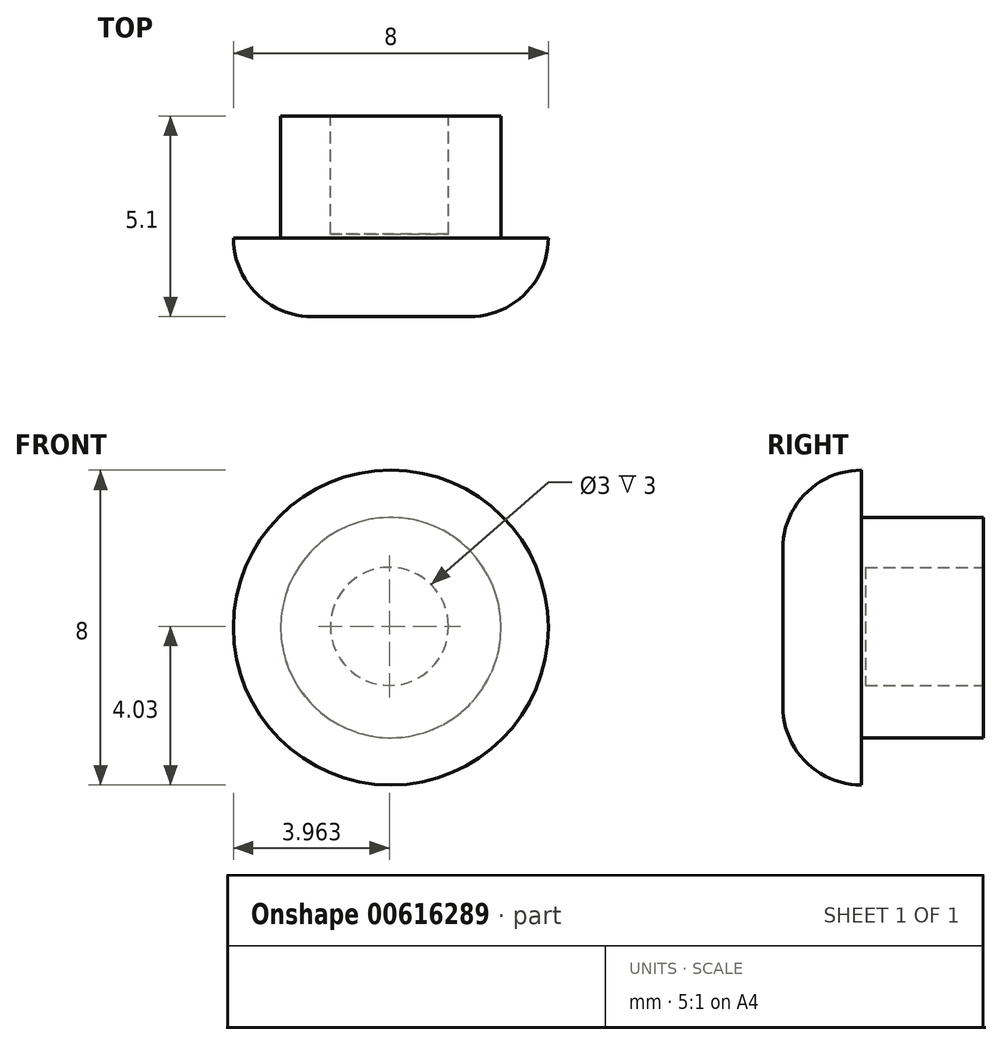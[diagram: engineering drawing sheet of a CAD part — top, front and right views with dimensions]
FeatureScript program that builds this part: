
annotation { "Feature Type Name" : "Feature", "Feature Type Description" : "" }
export const myFeature = defineFeature(function(context is Context, id is Id, definition is map)
    precondition{}
    {
        {
            var Q0;
            Q0=qCreatedBy(makeId("Front.planeOp"),FACE);
            var sketch = newSketch(context, id + "F0", { "sketchPlane" : qUnion([Q0])});
            skCircle(sketch, "E0", {"center": v(0, 0) * mm, "radius": 4 * mm});
            skSolve(sketch);
        }
        {
            var Q0;
            Q0=makeQuery(id+"F0.imprint","IMPRINT",FACE,{"disambiguationData":[TD([[makeQuery(id+"F0.imprint","IMPRINT",EDGE,{"derivedFrom":sQuery(id+"F0.wireOp",EDGE,"E0")}),1.0]])]});
            extrude(context, id + "F1", {"entities" : qUnion([Q0]), "depth" : 2 * mm, "offsetDistance" : 25 * mm});
        }
        {
            var Q0;
            Q0=makeQuery(id+"F1.opExtrude","CAP_EDGE",EDGE,{"disambiguationData":[OSD([sQuery(id+"F0.wireOp",EDGE,"E0")])],"isStart":false});
            fillet(context, id + "F2", {"entities" : qUnion([Q0]), "radius" : 2 * mm, "tangentPropagation" : true, "allowEdgeOverflow" : false});
        }
        {
            var Q0;
            Q0=makeQuery(id+"F1.opExtrude","CAP_FACE",FACE,{"disambiguationData":[OSD([sQuery(id+"F0.wireOp",EDGE,"E0")])],"isStart":true});
            var sketch = newSketch(context, id + "F3", { "sketchPlane" : qUnion([Q0])});
            skCircle(sketch, "E1", {"center": v(0, 0) * mm, "radius": 2.8 * mm});
            skSolve(sketch);
        }
        {
            var Q0;
            Q0=makeQuery(id+"F3.imprint","IMPRINT",FACE,{"disambiguationData":[TD([[makeQuery(id+"F3.imprint","IMPRINT",EDGE,{"derivedFrom":sQuery(id+"F3.wireOp",EDGE,"E1")}),1.0]])]});
            extrude(context, id + "F4", {"entities" : qUnion([Q0]), "operationType" : NewBodyOperationType.ADD, "depth" : 3.1 * mm, "offsetDistance" : 25 * mm});
        }
        {
            var Q0;
            Q0=makeQuery(id+"F4.opExtrude","CAP_FACE",FACE,{"disambiguationData":[OSD([sQuery(id+"F3.wireOp",EDGE,"E1")])],"isStart":false});
            var sketch = newSketch(context, id + "F5", { "sketchPlane" : qUnion([Q0])});
            skCircle(sketch, "E2", {"center": v(0.04, 0.03) * mm, "radius": 1.5 * mm});
            skSolve(sketch);
        }
        {
            var Q0;
            Q0=makeQuery(id+"F5.imprint","IMPRINT",FACE,{"disambiguationData":[TD([[makeQuery(id+"F5.imprint","IMPRINT",EDGE,{"derivedFrom":sQuery(id+"F5.wireOp",EDGE,"E2")}),1.0]])]});
            extrude(context, id + "F6", {"entities" : qUnion([Q0]), "operationType" : NewBodyOperationType.REMOVE, "oppositeDirection" : true, "depth" : 3 * mm, "offsetDistance" : 25 * mm});
        }
    });
